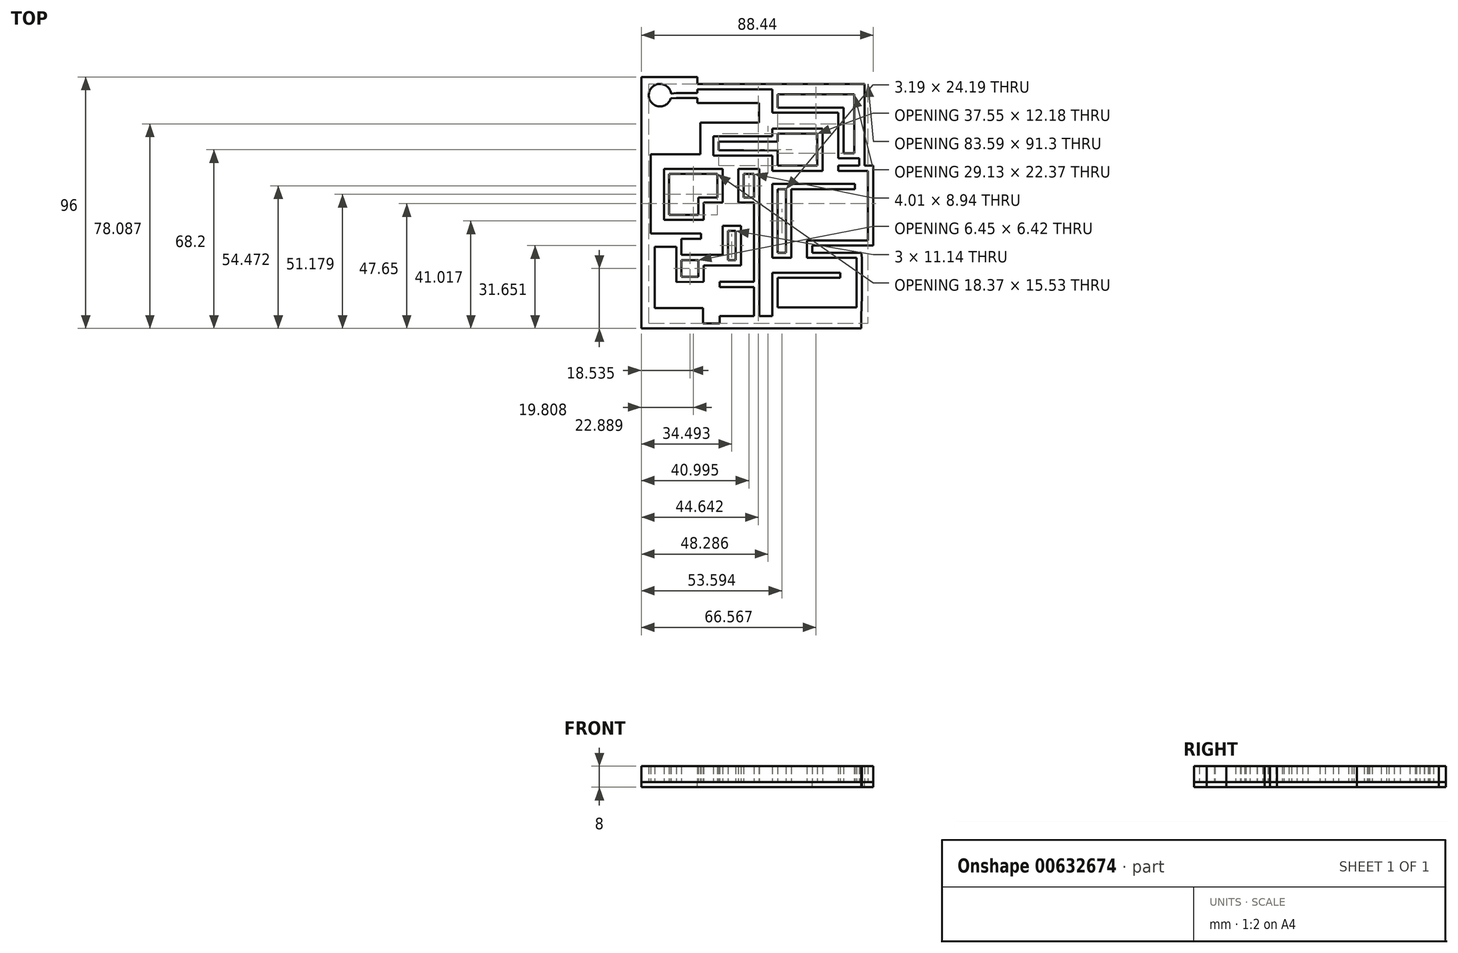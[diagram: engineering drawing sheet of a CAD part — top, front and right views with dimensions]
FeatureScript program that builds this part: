
annotation { "Feature Type Name" : "Feature", "Feature Type Description" : "" }
export const myFeature = defineFeature(function(context is Context, id is Id, definition is map)
    precondition{}
    {
        {
            var Q0;
            Q0=qCreatedBy(makeId("Top.planeOp"),FACE);
            var sketch = newSketch(context, id + "F0", { "sketchPlane" : qUnion([Q0])});
            skLineSegment(sketch, "E0.bottom", {"start": v(-50, 50) * mm, "end": v(50, 50) * mm});
            skLineSegment(sketch, "E0.top", {"start": v(-50, -50) * mm, "end": v(-26.52, -50) * mm});
            skLineSegment(sketch, "E0.left", {"start": v(-50, 50) * mm, "end": v(-50, -50) * mm});
            skPoint(sketch, "E0.middle", {"position": v(0, 0) * mm});
            skLineSegment(sketch, "E1", {"start": v(35.85, -48) * mm, "end": v(35.85, -43.22) * mm});
            skLineSegment(sketch, "E2.5", {"start": v(2, 43.27) * mm, "end": v(2, 34.3) * mm});
            skLineSegment(sketch, "E2.6", {"start": v(2, 25.31) * mm, "end": v(-20.49, 25.31) * mm});
            skLineSegment(sketch, "E3", {"start": v(-20.49, 25.31) * mm, "end": v(-20.49, 17.94) * mm});
            skLineSegment(sketch, "E4", {"start": v(-20.49, 17.94) * mm, "end": v(-2.51, 17.94) * mm});
            skLineSegment(sketch, "E5", {"start": v(-2.51, 17.94) * mm, "end": v(2, 17.94) * mm});
            skLineSegment(sketch, "E6", {"start": v(2, 17.94) * mm, "end": v(2, 12.1) * mm});
            skLineSegment(sketch, "E7", {"start": v(2, 12.1) * mm, "end": v(21.06, 12.1) * mm});
            skLineSegment(sketch, "E8", {"start": v(38.44, 12.1) * mm, "end": v(38.44, 3.69) * mm});
            skLineSegment(sketch, "E9.1", {"start": v(-3, 13.1) * mm, "end": v(-3, 12.94) * mm});
            skLineSegment(sketch, "E9.5", {"start": v(-26.62, 38.07) * mm, "end": v(-3.2, 38.07) * mm});
            skLineSegment(sketch, "E9.6", {"start": v(-3.2, 38.07) * mm, "end": v(-3.2, 30.51) * mm});
            skLineSegment(sketch, "E9.7", {"start": v(-3.2, 30.51) * mm, "end": v(-25.49, 30.51) * mm});
            skLineSegment(sketch, "E10", {"start": v(-25.29, 12.94) * mm, "end": v(-17, 12.94) * mm});
            skLineSegment(sketch, "E11", {"start": v(-28.73, -6.59) * mm, "end": v(-39.38, -6.59) * mm});
            skLineSegment(sketch, "E12", {"start": v(-39.38, -6.59) * mm, "end": v(-39.38, 12.94) * mm});
            skLineSegment(sketch, "E13", {"start": v(2, -43.22) * mm, "end": v(-18.08, -43.22) * mm});
            skLineSegment(sketch, "E14", {"start": v(-18.08, -43.22) * mm, "end": v(-18.08, -48) * mm});
            skLineSegment(sketch, "E15", {"start": v(-3, 13.1) * mm, "end": v(-3, 0) * mm});
            skLineSegment(sketch, "E16", {"start": v(-3, 0) * mm, "end": v(-11, 0) * mm});
            skLineSegment(sketch, "E17", {"start": v(-24.24, 0) * mm, "end": v(-24.24, -2.75) * mm});
            skLineSegment(sketch, "E18", {"start": v(-3, -2.75) * mm, "end": v(-3, -30.2) * mm});
            skLineSegment(sketch, "E19", {"start": v(-3, -30.2) * mm, "end": v(-8.04, -30.2) * mm});
            skLineSegment(sketch, "E20", {"start": v(-24.52, -42.24) * mm, "end": v(-24.52, -43.24) * mm});
            skLineSegment(sketch, "E21", {"start": v(2, 7.1) * mm, "end": v(2, -21.08) * mm});
            skLineSegment(sketch, "E22", {"start": v(2, -26.68) * mm, "end": v(2, -43.22) * mm});
            skLineSegment(sketch, "E23", {"start": v(2, -21.08) * mm, "end": v(9.19, -21.08) * mm});
            skLineSegment(sketch, "E24", {"start": v(34.05, -21.08) * mm, "end": v(34.05, -26.68) * mm});
            skLineSegment(sketch, "E25", {"start": v(2, -26.68) * mm, "end": v(27.88, -26.68) * mm});
            skLineSegment(sketch, "E26", {"start": v(27.88, -26.68) * mm, "end": v(27.88, -28.68) * mm});
            skLineSegment(sketch, "E27", {"start": v(34.05, -26.68) * mm, "end": v(34.05, -35.77) * mm});
            skLineSegment(sketch, "E28", {"start": v(34.05, -35.77) * mm, "end": v(34.05, -40) * mm});
            skLineSegment(sketch, "E29", {"start": v(34.05, -40) * mm, "end": v(4, -40) * mm});
            skLineSegment(sketch, "E30.1", {"start": v(-44.38, -11.59) * mm, "end": v(-44.38, 18.44) * mm});
            skLineSegment(sketch, "E31.0", {"start": v(-25.49, 25.31) * mm, "end": v(-25.49, 18.44) * mm});
            skLineSegment(sketch, "E32", {"start": v(-25.49, 25.31) * mm, "end": v(-25.49, 30.51) * mm});
            skLineSegment(sketch, "E33", {"start": v(-17, -8.78) * mm, "end": v(-17, -14.81) * mm});
            skLineSegment(sketch, "E34", {"start": v(-44.92, -14.81) * mm, "end": v(-44.92, -35.22) * mm});
            skLineSegment(sketch, "E35", {"start": v(-44.92, -35.22) * mm, "end": v(-44.92, -42.24) * mm});
            skLineSegment(sketch, "E36", {"start": v(-44.92, -42.24) * mm, "end": v(-24.52, -42.24) * mm});
            skLineSegment(sketch, "E37", {"start": v(-17, -14.81) * mm, "end": v(-17, -19.9) * mm});
            skLineSegment(sketch, "E38", {"start": v(-17, -19.9) * mm, "end": v(-34.69, -19.9) * mm});
            skLineSegment(sketch, "E39", {"start": v(-34.69, -19.9) * mm, "end": v(-34.69, -30.35) * mm});
            skLineSegment(sketch, "E40", {"start": v(-34.69, -30.35) * mm, "end": v(-24.52, -30.2) * mm});
            skLineSegment(sketch, "E41", {"start": v(2, 12.1) * mm, "end": v(2, 7.1) * mm});
            skLineSegment(sketch, "E42", {"start": v(-17, -8.78) * mm, "end": v(-10, -8.78) * mm});
            skLineSegment(sketch, "E43", {"start": v(-10, -8.78) * mm, "end": v(-10, -23.92) * mm});
            skLineSegment(sketch, "E44", {"start": v(-10, -23.92) * mm, "end": v(-24.24, -23.92) * mm});
            skLineSegment(sketch, "E45", {"start": v(-34.69, -19.9) * mm, "end": v(-34.69, -14.81) * mm});
            skLineSegment(sketch, "E46", {"start": v(-8.04, -30.2) * mm, "end": v(-18.08, -30.2) * mm});
            skLineSegment(sketch, "E47", {"start": v(9.19, 5.1) * mm, "end": v(9.19, -21.08) * mm});
            skLineSegment(sketch, "E48.trimOffspring", {"start": v(15.19, -21.08) * mm, "end": v(34.05, -21.08) * mm});
            skLineSegment(sketch, "E49", {"start": v(2, 34.3) * mm, "end": v(27.06, 34.3) * mm});
            skLineSegment(sketch, "E50", {"start": v(27.06, 34.3) * mm, "end": v(27.06, 16.9) * mm});
            skLineSegment(sketch, "E51.0", {"start": v(21.06, 28.3) * mm, "end": v(21.06, 12.1) * mm});
            skLineSegment(sketch, "E51.1", {"start": v(2, 28.3) * mm, "end": v(21.06, 28.3) * mm});
            skLineSegment(sketch, "E52.trimOffspring", {"start": v(2, 28.3) * mm, "end": v(2, 25.31) * mm});
            skLineSegment(sketch, "E53.trimOffspring", {"start": v(27.06, 12.1) * mm, "end": v(38.44, 12.1) * mm});
            skLineSegment(sketch, "E54", {"start": v(-26.62, 38.07) * mm, "end": v(-26.62, 39.2) * mm});
            skLineSegment(sketch, "E55", {"start": v(2, 43.27) * mm, "end": v(-20.5, 43.27) * mm});
            skLineSegment(sketch, "E56", {"start": v(35.1, 16.9) * mm, "end": v(27.06, 16.9) * mm});
            skLineSegment(sketch, "E57.trimOffspring", {"start": v(27.06, 12.1) * mm, "end": v(27.06, 12.08) * mm});
            skLineSegment(sketch, "E58", {"start": v(38.44, 3.69) * mm, "end": v(38.44, -14.38) * mm});
            skLineSegment(sketch, "E59", {"start": v(38.44, -14.38) * mm, "end": v(15.19, -14.38) * mm});
            skLineSegment(sketch, "E60.trimOffspring", {"start": v(15.19, -14.38) * mm, "end": v(15.19, -21.08) * mm});
            skLineSegment(sketch, "E61", {"start": v(-17, 0) * mm, "end": v(-17, 12.94) * mm});
            skLineSegment(sketch, "E62.0", {"start": v(-11, 0) * mm, "end": v(-11, 12.94) * mm});
            skLineSegment(sketch, "E63.trimOffspring", {"start": v(-17, 0) * mm, "end": v(-24.24, 0) * mm});
            skLineSegment(sketch, "E64.trimOffspring", {"start": v(-11, 12.94) * mm, "end": v(-3, 12.94) * mm});
            skLineSegment(sketch, "E65", {"start": v(-28.73, -6.59) * mm, "end": v(-24.24, -6.59) * mm});
            skLineSegment(sketch, "E66.0", {"start": v(-27.49, 25.31) * mm, "end": v(-27.49, 20.44) * mm});
            skLineSegment(sketch, "E66.1", {"start": v(-27.49, 25.31) * mm, "end": v(-27.49, 32.51) * mm});
            skLineSegment(sketch, "E66.2", {"start": v(-28.62, 36.07) * mm, "end": v(-28.62, 38.07) * mm});
            skLineSegment(sketch, "E66.3", {"start": v(-28.62, 36.07) * mm, "end": v(-5.2, 36.07) * mm});
            skLineSegment(sketch, "E66.4", {"start": v(-5.2, 36.07) * mm, "end": v(-5.2, 32.51) * mm});
            skLineSegment(sketch, "E66.5", {"start": v(-5.2, 32.51) * mm, "end": v(-27.49, 32.51) * mm});
            skCircle(sketch, "E67", {"center": v(42.5, -41.37) * mm, "radius": 1.37 * mm});
            skCircle(sketch, "E68", {"center": v(42.5, -41.37) * mm, "radius": 0.87 * mm});
            skLineSegment(sketch, "E69.0", {"start": v(-46.38, -13.59) * mm, "end": v(-46.38, 18.44) * mm});
            skLineSegment(sketch, "E70.4", {"start": v(-46.38, -44.24) * mm, "end": v(-26.52, -44.24) * mm});
            skLineSegment(sketch, "E71", {"start": v(-26.52, -50) * mm, "end": v(-24.52, -50) * mm});
            skCircle(sketch, "E72", {"center": v(42.5, -41.37) * mm, "radius": 2.87 * mm});
            skLineSegment(sketch, "E73", {"start": v(-46.38, 18.44) * mm, "end": v(-46.38, 20.47) * mm});
            skLineSegment(sketch, "E74", {"start": v(-46.38, -13.59) * mm, "end": v(-46.38, -44.24) * mm});
            skPoint(sketch, "E75.orphan", {"position": v(-46.92, -44.24) * mm});
            skLineSegment(sketch, "E76", {"start": v(-44.32, 20.44) * mm, "end": v(-46.38, 20.47) * mm});
            skLineSegment(sketch, "E77", {"start": v(-44.32, 20.44) * mm, "end": v(-27.49, 20.44) * mm});
            skLineSegment(sketch, "E78", {"start": v(-24.24, -6.59) * mm, "end": v(-24.24, -2.75) * mm});
            skLineSegment(sketch, "E79.trimOffspring", {"start": v(-25.49, 17.95) * mm, "end": v(-25.49, 17.94) * mm});
            skLineSegment(sketch, "E80.0", {"start": v(-48, 48) * mm, "end": v(-28.62, 48) * mm});
            skLineSegment(sketch, "E80.1", {"start": v(-48, 48) * mm, "end": v(-48, -48) * mm});
            skLineSegment(sketch, "E80.2", {"start": v(-48, -48) * mm, "end": v(48, -48) * mm});
            skLineSegment(sketch, "E80.3", {"start": v(48, 48) * mm, "end": v(48, -48) * mm});
            skLineSegment(sketch, "E81.trimOffspring", {"start": v(-26.62, 48) * mm, "end": v(48, 48) * mm});
            skLineSegment(sketch, "E82", {"start": v(-44.38, 18.44) * mm, "end": v(-25.49, 18.44) * mm});
            skLineSegment(sketch, "E83.0", {"start": v(2, 45.27) * mm, "end": v(-20.5, 45.27) * mm});
            skLineSegment(sketch, "E83.1", {"start": v(2, 45.27) * mm, "end": v(12.72, 45.27) * mm});
            skLineSegment(sketch, "E83.2", {"start": v(37.1, 45.27) * mm, "end": v(37.1, 16.9) * mm});
            skLineSegment(sketch, "E83.3", {"start": v(34.15, 45.27) * mm, "end": v(37.1, 45.27) * mm});
            skLineSegment(sketch, "E83.4", {"start": v(15.13, 45.27) * mm, "end": v(34.15, 45.27) * mm});
            skLineSegment(sketch, "E83.5", {"start": v(12.72, 45.27) * mm, "end": v(15.13, 45.27) * mm});
            skLineSegment(sketch, "E84", {"start": v(37.1, 12.08) * mm, "end": v(37.1, 12.1) * mm});
            skLineSegment(sketch, "E85.1", {"start": v(-37.38, -4.59) * mm, "end": v(-37.38, 10.94) * mm});
            skLineSegment(sketch, "E85.2", {"start": v(-25.32, 10.94) * mm, "end": v(-19, 10.94) * mm});
            skLineSegment(sketch, "E85.3", {"start": v(-28.73, -4.59) * mm, "end": v(-37.38, -4.59) * mm});
            skLineSegment(sketch, "E85.4", {"start": v(-28.73, -4.59) * mm, "end": v(-26.24, -4.59) * mm});
            skLineSegment(sketch, "E85.5", {"start": v(-19, 2) * mm, "end": v(-19, 10.94) * mm});
            skLineSegment(sketch, "E85.6", {"start": v(-19, 2) * mm, "end": v(-26.24, 2) * mm});
            skLineSegment(sketch, "E85.7", {"start": v(-26.24, 2) * mm, "end": v(-26.24, -2.75) * mm});
            skLineSegment(sketch, "E85.8", {"start": v(-26.24, -4.59) * mm, "end": v(-26.24, -2.75) * mm});
            skLineSegment(sketch, "E86", {"start": v(37.1, 12.1) * mm, "end": v(37.1, 12.08) * mm});
            skLineSegment(sketch, "E87.0", {"start": v(19.06, 22.3) * mm, "end": v(19.06, 14.1) * mm});
            skLineSegment(sketch, "E87.2", {"start": v(-2.51, 19.94) * mm, "end": v(4, 19.94) * mm});
            skLineSegment(sketch, "E87.3", {"start": v(4, 19.94) * mm, "end": v(4, 14.1) * mm});
            skLineSegment(sketch, "E87.4", {"start": v(4, 14.1) * mm, "end": v(19.06, 14.1) * mm});
            skLineSegment(sketch, "E88.0", {"start": v(-18.49, 23.31) * mm, "end": v(-18.49, 17.94) * mm});
            skLineSegment(sketch, "E88.1", {"start": v(4, 23.31) * mm, "end": v(-18.49, 23.31) * mm});
            skLineSegment(sketch, "E88.2", {"start": v(4, 26.3) * mm, "end": v(4, 23.31) * mm});
            skLineSegment(sketch, "E89.0", {"start": v(4, 26.3) * mm, "end": v(19.06, 26.3) * mm});
            skLineSegment(sketch, "E90.0", {"start": v(-18.49, 19.94) * mm, "end": v(-2.51, 19.94) * mm});
            skLineSegment(sketch, "E91.0", {"start": v(27.06, 14.1) * mm, "end": v(35.1, 14.1) * mm});
            skLineSegment(sketch, "E92.0", {"start": v(40.44, 3.69) * mm, "end": v(40.44, -14.38) * mm});
            skLineSegment(sketch, "E92.1", {"start": v(40.44, 12.1) * mm, "end": v(40.44, 3.69) * mm});
            skLineSegment(sketch, "E93", {"start": v(40.44, 14.1) * mm, "end": v(40.44, 12.1) * mm});
            skLineSegment(sketch, "E94.0", {"start": v(17.19, -16.38) * mm, "end": v(17.19, -19.08) * mm});
            skLineSegment(sketch, "E94.1", {"start": v(38.44, -16.38) * mm, "end": v(17.19, -16.38) * mm});
            skLineSegment(sketch, "E95.0", {"start": v(17.19, -19.08) * mm, "end": v(34.05, -19.08) * mm});
            skLineSegment(sketch, "E96", {"start": v(40.44, -14.38) * mm, "end": v(40.44, -16.38) * mm});
            skLineSegment(sketch, "E97", {"start": v(40.44, -16.38) * mm, "end": v(38.44, -16.38) * mm});
            skLineSegment(sketch, "E98.1", {"start": v(36.05, -26.68) * mm, "end": v(36.05, -35.77) * mm});
            skLineSegment(sketch, "E98.2", {"start": v(36.05, -21.08) * mm, "end": v(36.05, -26.68) * mm});
            skLineSegment(sketch, "E99", {"start": v(34.05, -19.08) * mm, "end": v(35.9, -19.08) * mm});
            skLineSegment(sketch, "E100", {"start": v(35.9, -19.08) * mm, "end": v(36.05, -21.08) * mm});
            skLineSegment(sketch, "E101", {"start": v(2, -43.22) * mm, "end": v(35.85, -43.22) * mm});
            skLineSegment(sketch, "E102", {"start": v(36.05, -35.77) * mm, "end": v(35.85, -43.22) * mm});
            skLineSegment(sketch, "E103.0", {"start": v(33.85, -48) * mm, "end": v(33.85, -45.22) * mm});
            skLineSegment(sketch, "E103.1", {"start": v(2, -45.22) * mm, "end": v(33.85, -45.22) * mm});
            skLineSegment(sketch, "E103.2", {"start": v(2, -45.22) * mm, "end": v(-16.08, -45.22) * mm});
            skLineSegment(sketch, "E103.3", {"start": v(-16.08, -45.22) * mm, "end": v(-16.08, -48) * mm});
            skCircle(sketch, "E104", {"center": v(42.5, -41.37) * mm, "radius": 4.65 * mm});
            skCircle(sketch, "E105", {"center": v(42.5, -41.37) * mm, "radius": 4.04 * mm});
            skCircle(sketch, "E106", {"center": v(42.5, -41.37) * mm, "radius": 2.12 * mm});
            skLineSegment(sketch, "E107.0", {"start": v(-32.69, -28.32) * mm, "end": v(-26.44, -28.24) * mm});
            skLineSegment(sketch, "E107.1", {"start": v(-32.69, -21.9) * mm, "end": v(-32.69, -28.32) * mm});
            skLineSegment(sketch, "E108.2", {"start": v(-15, -10.78) * mm, "end": v(-12, -10.78) * mm});
            skLineSegment(sketch, "E109.0", {"start": v(-12, -10.78) * mm, "end": v(-12, -21.92) * mm});
            skLineSegment(sketch, "E110", {"start": v(-24.24, -24.07) * mm, "end": v(-24.24, -30.19) * mm});
            skLineSegment(sketch, "E111", {"start": v(-24.24, -30.19) * mm, "end": v(-24.52, -30.2) * mm});
            skLineSegment(sketch, "E112", {"start": v(-24.24, -24.07) * mm, "end": v(-24.24, -23.92) * mm});
            skLineSegment(sketch, "E113.0", {"start": v(-26.24, -24.07) * mm, "end": v(-26.24, -28.24) * mm});
            skLineSegment(sketch, "E114", {"start": v(-26.26, -23.92) * mm, "end": v(-26.24, -24.07) * mm});
            skLineSegment(sketch, "E115", {"start": v(-26.44, -28.24) * mm, "end": v(-26.24, -28.24) * mm});
            skLineSegment(sketch, "E116", {"start": v(27.06, 14.1) * mm, "end": v(27.06, 12.1) * mm});
            skLineSegment(sketch, "E117.0", {"start": v(-10.04, -32.2) * mm, "end": v(-18.08, -32.2) * mm});
            skLineSegment(sketch, "E117.1", {"start": v(-10.04, -43.22) * mm, "end": v(-10.04, -32.2) * mm});
            skLineSegment(sketch, "E118", {"start": v(-18.08, -30.2) * mm, "end": v(-18.08, -32.2) * mm});
            skLineSegment(sketch, "E119", {"start": v(-3, -2.75) * mm, "end": v(-3, 0) * mm});
            skPoint(sketch, "E120.start.orphan", {"position": v(-8.04, -43.22) * mm});
            skLineSegment(sketch, "E121", {"start": v(-3, -30.2) * mm, "end": v(-3, -43.22) * mm});
            skLineSegment(sketch, "E122.0", {"start": v(-5, -2.75) * mm, "end": v(-5, -30.2) * mm});
            skLineSegment(sketch, "E123", {"start": v(-5, -2.75) * mm, "end": v(-5, 0) * mm});
            skLineSegment(sketch, "E124", {"start": v(-12, -21.92) * mm, "end": v(-15, -21.92) * mm});
            skPoint(sketch, "E108.0.end.orphan", {"position": v(-15, -19.9) * mm});
            skLineSegment(sketch, "E125", {"start": v(-15, -10.78) * mm, "end": v(-15, -21.92) * mm});
            skLineSegment(sketch, "E126", {"start": v(-32.69, -21.9) * mm, "end": v(-26.24, -21.9) * mm});
            skLineSegment(sketch, "E127", {"start": v(-26.24, -21.9) * mm, "end": v(-26.26, -23.92) * mm});
            skLineSegment(sketch, "E128.0", {"start": v(-32.69, -19.9) * mm, "end": v(-32.69, -14.81) * mm});
            skLineSegment(sketch, "E129.0", {"start": v(33.44, 5.1) * mm, "end": v(28.44, 5.1) * mm});
            skLineSegment(sketch, "E130.0", {"start": v(4, 5.1) * mm, "end": v(4, -19.08) * mm});
            skLineSegment(sketch, "E130.1", {"start": v(4, -19.08) * mm, "end": v(7.19, -19.08) * mm});
            skLineSegment(sketch, "E130.2", {"start": v(7.19, 5.1) * mm, "end": v(7.19, -19.08) * mm});
            skLineSegment(sketch, "E131.0", {"start": v(30.44, 5.1) * mm, "end": v(28.44, 5.1) * mm});
            skLineSegment(sketch, "E132.trimOffspring", {"start": v(7.19, 5.1) * mm, "end": v(4, 5.1) * mm});
            skLineSegment(sketch, "E133.0", {"start": v(7, 36.3) * mm, "end": v(29.06, 36.3) * mm});
            skLineSegment(sketch, "E133.1", {"start": v(29.06, 36.3) * mm, "end": v(29.06, 18.9) * mm});
            skLineSegment(sketch, "E133.2", {"start": v(33.13, 18.9) * mm, "end": v(29.06, 18.9) * mm});
            skLineSegment(sketch, "E134.0", {"start": v(4, 41.27) * mm, "end": v(4, 36.3) * mm});
            skLineSegment(sketch, "E134.1", {"start": v(4, 41.27) * mm, "end": v(12.72, 41.27) * mm});
            skLineSegment(sketch, "E134.2", {"start": v(12.72, 41.27) * mm, "end": v(15.13, 41.27) * mm});
            skLineSegment(sketch, "E134.3", {"start": v(15.13, 41.27) * mm, "end": v(33.13, 41.27) * mm});
            skLineSegment(sketch, "E135.0", {"start": v(33.13, 41.27) * mm, "end": v(33.13, 18.9) * mm});
            skLineSegment(sketch, "E136", {"start": v(7, 36.3) * mm, "end": v(4, 36.3) * mm});
            skLineSegment(sketch, "E137.0", {"start": v(-9, 10.94) * mm, "end": v(-5, 10.94) * mm});
            skLineSegment(sketch, "E137.1", {"start": v(-9, 2) * mm, "end": v(-9, 10.94) * mm});
            skLineSegment(sketch, "E137.2", {"start": v(-5, 2) * mm, "end": v(-9, 2) * mm});
            skLineSegment(sketch, "E138.0", {"start": v(-5, 13.1) * mm, "end": v(-5, 12.94) * mm});
            skLineSegment(sketch, "E139.trimOffspring", {"start": v(-5, 10.94) * mm, "end": v(-5, 2) * mm});
            skLineSegment(sketch, "E140", {"start": v(19.06, 22.3) * mm, "end": v(19.06, 26.3) * mm});
            skLineSegment(sketch, "E141.0", {"start": v(-42.92, -16.81) * mm, "end": v(-42.92, -35.22) * mm});
            skLineSegment(sketch, "E141.1", {"start": v(-34.69, -16.81) * mm, "end": v(-42.92, -16.81) * mm});
            skLineSegment(sketch, "E142.0", {"start": v(-42.92, -40.24) * mm, "end": v(-24.52, -40.24) * mm});
            skLineSegment(sketch, "E142.1", {"start": v(-42.92, -35.22) * mm, "end": v(-42.92, -40.24) * mm});
            skLineSegment(sketch, "E143", {"start": v(-24.52, -42.24) * mm, "end": v(-24.52, -40.24) * mm});
            skLineSegment(sketch, "E144.0", {"start": v(-25.24, -13.81) * mm, "end": v(-44.92, -13.81) * mm});
            skLineSegment(sketch, "E145.0", {"start": v(-25.24, -11.59) * mm, "end": v(-25.24, -13.81) * mm});
            skLineSegment(sketch, "E146.0", {"start": v(4, -28.68) * mm, "end": v(27.88, -28.68) * mm});
            skLineSegment(sketch, "E147.0", {"start": v(-5, -32.2) * mm, "end": v(-5, -43.22) * mm});
            skLineSegment(sketch, "E148.0", {"start": v(-8.04, -32.2) * mm, "end": v(-18.08, -32.2) * mm});
            skLineSegment(sketch, "E148.1", {"start": v(-5, -32.2) * mm, "end": v(-8.04, -32.2) * mm});
            skLineSegment(sketch, "E149", {"start": v(-44.92, -14.81) * mm, "end": v(-44.92, -13.81) * mm});
            skLineSegment(sketch, "E150", {"start": v(-34.69, -14.81) * mm, "end": v(-34.69, -13.81) * mm});
            skLineSegment(sketch, "E151", {"start": v(-32.69, -14.81) * mm, "end": v(-32.69, -13.81) * mm});
            skLineSegment(sketch, "E152.trimOffspring", {"start": v(37.1, 14.1) * mm, "end": v(40.44, 14.1) * mm});
            skLineSegment(sketch, "E153.trimOffspring", {"start": v(35.13, 12.1) * mm, "end": v(35.13, 12.08) * mm});
            skLineSegment(sketch, "E154.trimOffspring", {"start": v(37.1, 14.1) * mm, "end": v(37.1, 16.9) * mm});
            skArc(sketch, "E155", {"start": v(-35.02, 43.27) * mm, "mid": v(-47.16, 41.4) * mm, "end": v(-35.34, 38.07) * mm});
            skLineSegment(sketch, "E156", {"start": v(-34.66, 41.87) * mm, "end": v(-28.62, 41.87) * mm});
            skLineSegment(sketch, "E157.trimOffspring", {"start": v(-28.62, 43.27) * mm, "end": v(-28.62, 48) * mm});
            skLineSegment(sketch, "E158", {"start": v(-26.62, 41.93) * mm, "end": v(-26.62, 43.27) * mm});
            skLineSegment(sketch, "E159.0", {"start": v(-34.66, 39.87) * mm, "end": v(-28.62, 39.87) * mm});
            skLineSegment(sketch, "E160", {"start": v(-26.62, 39.2) * mm, "end": v(-26.62, 39.87) * mm});
            skLineSegment(sketch, "E161.0", {"start": v(35.1, 14.1) * mm, "end": v(35.1, 16.9) * mm});
            skLineSegment(sketch, "E162.0", {"start": v(4, -28.68) * mm, "end": v(4, -40) * mm});
            skLineSegment(sketch, "E163.0", {"start": v(-25.24, -11.81) * mm, "end": v(-44.38, -11.81) * mm});
            skLineSegment(sketch, "E164", {"start": v(33.44, 7.1) * mm, "end": v(33.44, 5.1) * mm});
            skLineSegment(sketch, "E165.0", {"start": v(7.19, 7.1) * mm, "end": v(4, 7.1) * mm});
            skLineSegment(sketch, "E166.0", {"start": v(30.44, 7.1) * mm, "end": v(9.19, 7.1) * mm});
            skLineSegment(sketch, "E167", {"start": v(2, 7.1) * mm, "end": v(4, 7.1) * mm});
            skLineSegment(sketch, "E168", {"start": v(7.19, 7.1) * mm, "end": v(9.19, 7.1) * mm});
            skLineSegment(sketch, "E169", {"start": v(30.44, 7.1) * mm, "end": v(33.44, 7.1) * mm});
            skLineSegment(sketch, "E170.trimOffspring", {"start": v(17.19, 5.1) * mm, "end": v(9.19, 5.1) * mm});
            skLineSegment(sketch, "E171.trimOffspring", {"start": v(17.19, 5.1) * mm, "end": v(15.19, 5.1) * mm});
            skLineSegment(sketch, "E172", {"start": v(17.19, 5.1) * mm, "end": v(28.44, 5.1) * mm});
            skArc(sketch, "E173.0", {"start": v(-36.64, 41.6) * mm, "mid": v(-45.15, 41.36) * mm, "end": v(-36.79, 39.77) * mm});
            skLineSegment(sketch, "E174", {"start": v(-28.62, 41.87) * mm, "end": v(-26.62, 41.87) * mm});
            skLineSegment(sketch, "E175", {"start": v(-26.62, 41.87) * mm, "end": v(-26.62, 41.93) * mm});
            skLineSegment(sketch, "E176.0", {"start": v(-28.62, 39.87) * mm, "end": v(-26.62, 39.87) * mm});
            skLineSegment(sketch, "E177", {"start": v(-44.38, -11.59) * mm, "end": v(-44.38, -11.81) * mm});
            skLineSegment(sketch, "E178", {"start": v(-26.52, -44.24) * mm, "end": v(-24.52, -44.24) * mm});
            skLineSegment(sketch, "E179", {"start": v(-24.52, -44.24) * mm, "end": v(-24.52, -43.24) * mm});
            skLineSegment(sketch, "E180", {"start": v(-25.32, 10.94) * mm, "end": v(-37.38, 10.94) * mm});
            skLineSegment(sketch, "E181.0", {"start": v(-25.32, 12.94) * mm, "end": v(-37.38, 12.94) * mm});
            skLineSegment(sketch, "E182", {"start": v(-37.38, 12.94) * mm, "end": v(-39.38, 12.94) * mm});
            skLineSegment(sketch, "E183", {"start": v(-36.64, 41.6) * mm, "end": v(-34.66, 41.87) * mm});
            skLineSegment(sketch, "E184", {"start": v(-36.79, 39.77) * mm, "end": v(-34.66, 39.87) * mm});
            skLineSegment(sketch, "E185", {"start": v(-25.32, 12.94) * mm, "end": v(-25.29, 12.94) * mm});
            skLineSegment(sketch, "E186", {"start": v(-28.62, 48) * mm, "end": v(-26.62, 48) * mm});
            skLineSegment(sketch, "E187.trimOffspring", {"start": v(-24.52, -50) * mm, "end": v(50, -50) * mm});
            skLineSegment(sketch, "E188.trimOffspring", {"start": v(42.13, -46) * mm, "end": v(42.88, -46) * mm});
            skLineSegment(sketch, "E189", {"start": v(-20.5, 45.27) * mm, "end": v(-26.62, 45.27) * mm});
            skLineSegment(sketch, "E190.0", {"start": v(-20.5, 43.27) * mm, "end": v(-26.62, 43.27) * mm});
            skLineSegment(sketch, "E191", {"start": v(-24.52, -44.24) * mm, "end": v(-24.52, -48) * mm});
            skLineSegment(sketch, "E192.0", {"start": v(-26.52, -44.24) * mm, "end": v(-26.52, -48) * mm});
            skLineSegment(sketch, "E193.0", {"start": v(-24.52, -46) * mm, "end": v(-18.08, -46) * mm});
            skLineSegment(sketch, "E194", {"start": v(-28.62, 38.07) * mm, "end": v(-35.34, 38.07) * mm});
            skLineSegment(sketch, "E195", {"start": v(-28.62, 43.27) * mm, "end": v(-35.02, 43.27) * mm});
            skPoint(sketch, "E196.start.orphan", {"position": v(-28.62, 39.2) * mm});
            skLineSegment(sketch, "E197.trimOffspring", {"start": v(-26.62, 45.27) * mm, "end": v(-26.62, 48) * mm});
            skSolve(sketch);
        }
        {
            var Q0;
            {var subQ0=sQuery(id+"F0.wireOp",EDGE,"E1");var subQ1=sQuery(id+"F0.wireOp",EDGE,"E0.top");var subQ2=makeQuery(id+"F0.imprint","INTERSECT",VERTEX,{"derivedFrom":[subQ1,subQ0]});Q0=makeQuery(id+"F0.imprint","IMPRINT",FACE,{"disambiguationData":[TD([[makeQuery(id+"F0.imprint","IMPRINT",EDGE,{"disambiguationData":[TD([[subQ2,1.0]])],"derivedFrom":subQ1}),1.0]])]});}
            var Q1;
            {var subQ0=sQuery(id+"F0.wireOp",EDGE,"E14");var subQ1=sQuery(id+"F0.wireOp",EDGE,"E0.top");var subQ2=makeQuery(id+"F0.imprint","INTERSECT",VERTEX,{"derivedFrom":[subQ1,subQ0]});Q1=makeQuery(id+"F0.imprint","IMPRINT",FACE,{"disambiguationData":[TD([[makeQuery(id+"F0.imprint","IMPRINT",EDGE,{"disambiguationData":[TD([[subQ2,-1.0]])],"derivedFrom":subQ1}),1.0]])]});}
            var Q2;
            {var subQ0=sQuery(id+"F0.wireOp",EDGE,"E103.0");var subQ1=sQuery(id+"F0.wireOp",EDGE,"E0.top");var subQ2=makeQuery(id+"F0.imprint","INTERSECT",VERTEX,{"derivedFrom":[subQ1,subQ0]});Q2=makeQuery(id+"F0.imprint","IMPRINT",FACE,{"disambiguationData":[TD([[makeQuery(id+"F0.imprint","IMPRINT",EDGE,{"disambiguationData":[TD([[subQ2,1.0]])],"derivedFrom":subQ1}),1.0]])]});}
            var Q3;
            {var subQ5=sQuery(id+"F0.wireOp",EDGE,"E101");Q3=makeQuery(id+"F0.imprint","IMPRINT",FACE,{"disambiguationData":[TD([[makeQuery(id+"F0.imprint","IMPRINT",EDGE,{"derivedFrom":subQ5}),-1.0]])]});}
            var Q4;
            Q4=makeQuery(id+"F0.imprint","IMPRINT",FACE,{"disambiguationData":[TD([[makeQuery(id+"F0.imprint","IMPRINT",EDGE,{"derivedFrom":sQuery(id+"F0.wireOp",EDGE,"E9.5")}),-1.0]])]});
            var Q5;
            Q5=makeQuery(id+"F0.imprint","IMPRINT",FACE,{"disambiguationData":[TD([[makeQuery(id+"F0.imprint","IMPRINT",EDGE,{"derivedFrom":sQuery(id+"F0.wireOp",EDGE,"E10")}),-1.0]])]});
            var Q6;
            Q6=makeQuery(id+"F0.imprint","IMPRINT",FACE,{"disambiguationData":[TD([[makeQuery(id+"F0.imprint","IMPRINT",EDGE,{"derivedFrom":sQuery(id+"F0.wireOp",EDGE,"E2.6")}),1.0]])]});
            var Q7;
            {var subQ0=sQuery(id+"F0.wireOp",EDGE,"E62.0");Q7=makeQuery(id+"F0.imprint","IMPRINT",FACE,{"disambiguationData":[TD([[makeQuery(id+"F0.imprint","IMPRINT",EDGE,{"derivedFrom":subQ0}),-1.0]])]});}
            var Q8;
            {var subQ2=sQuery(id+"F0.wireOp",EDGE,"E18");Q8=makeQuery(id+"F0.imprint","IMPRINT",FACE,{"disambiguationData":[TD([[makeQuery(id+"F0.imprint","IMPRINT",EDGE,{"derivedFrom":subQ2}),-1.0]])]});}
            var Q9;
            Q9=makeQuery(id+"F0.imprint","IMPRINT",FACE,{"disambiguationData":[TD([[makeQuery(id+"F0.imprint","IMPRINT",EDGE,{"derivedFrom":sQuery(id+"F0.wireOp",EDGE,"E33")}),1.0]])]});
            var Q10;
            Q10=makeQuery(id+"F0.imprint","IMPRINT",FACE,{"disambiguationData":[TD([[makeQuery(id+"F0.imprint","IMPRINT",EDGE,{"derivedFrom":sQuery(id+"F0.wireOp",EDGE,"E34")}),1.0]])]});
            var Q11;
            {var subQ5=sQuery(id+"F0.wireOp",EDGE,"E128.0");Q11=makeQuery(id+"F0.imprint","IMPRINT",FACE,{"disambiguationData":[TD([[makeQuery(id+"F0.imprint","IMPRINT",EDGE,{"derivedFrom":subQ5}),1.0]])]});}
            var Q12;
            Q12=makeQuery(id+"F0.imprint","IMPRINT",FACE,{"disambiguationData":[TD([[makeQuery(id+"F0.imprint","IMPRINT",EDGE,{"derivedFrom":sQuery(id+"F0.wireOp",EDGE,"E21")}),1.0]])]});
            var Q13;
            Q13=makeQuery(id+"F0.imprint","IMPRINT",FACE,{"disambiguationData":[TD([[makeQuery(id+"F0.imprint","IMPRINT",EDGE,{"derivedFrom":sQuery(id+"F0.wireOp",EDGE,"E2.5")}),1.0]])]});
            var Q14;
            {var subQ0=sQuery(id+"F0.wireOp",EDGE,"E46");Q14=makeQuery(id+"F0.imprint","IMPRINT",FACE,{"disambiguationData":[TD([[makeQuery(id+"F0.imprint","IMPRINT",EDGE,{"derivedFrom":subQ0}),1.0]])]});}
            var Q15;
            {var subQ0=sQuery(id+"F0.wireOp",EDGE,"E14");var subQ1=sQuery(id+"F0.wireOp",EDGE,"E0.top");var subQ2=makeQuery(id+"F0.imprint","INTERSECT",VERTEX,{"derivedFrom":[subQ1,subQ0]});Q15=makeQuery(id+"F0.imprint","IMPRINT",FACE,{"disambiguationData":[TD([[makeQuery(id+"F0.imprint","IMPRINT",EDGE,{"disambiguationData":[TD([[subQ2,1.0]])],"derivedFrom":subQ1}),1.0]])]});}
            var Q16;
            {var subQ0=sQuery(id+"F0.wireOp",EDGE,"E103.1");Q16=makeQuery(id+"F0.imprint","IMPRINT",FACE,{"disambiguationData":[TD([[makeQuery(id+"F0.imprint","IMPRINT",EDGE,{"derivedFrom":subQ0}),-1.0]])]});}
            var Q17;
            Q17=makeQuery(id+"F0.imprint","IMPRINT",FACE,{"disambiguationData":[TD([[makeQuery(id+"F0.imprint","IMPRINT",EDGE,{"derivedFrom":sQuery(id+"F0.wireOp",EDGE,"E66.0")}),-1.0]])]});
            var Q18;
            Q18=makeQuery(id+"F0.imprint","IMPRINT",FACE,{"disambiguationData":[TD([[makeQuery(id+"F0.imprint","IMPRINT",EDGE,{"derivedFrom":sQuery(id+"F0.wireOp",EDGE,"E155")}),1.0]])]});
            var Q19;
            {var subQ3=sQuery(id+"F0.wireOp",EDGE,"d1deb05d-b4d8-4f16-9e59-166c224445ac.0");Q19=makeQuery(id+"F0.imprint","IMPRINT",FACE,{"disambiguationData":[TD([[makeQuery(id+"F0.imprint","IMPRINT",EDGE,{"derivedFrom":subQ3}),-1.0]])]});}
            var Q20;
            Q20=makeQuery(id+"F0.imprint","IMPRINT",FACE,{"disambiguationData":[TD([[makeQuery(id+"F0.imprint","IMPRINT",EDGE,{"derivedFrom":sQuery(id+"F0.wireOp",EDGE,"ZVYSHCS1-2Een-s850-w6lb-LcxjED9iCilX")}),-1.0]])]});
            var Q21;
            Q21=makeQuery(id+"F0.imprint","IMPRINT",FACE,{"disambiguationData":[TD([[makeQuery(id+"F0.imprint","IMPRINT",EDGE,{"derivedFrom":sQuery(id+"F0.wireOp",EDGE,"E157.trimOffspring")}),-1.0]])]});
            var Q22;
            {var subQ3=sQuery(id+"F0.wireOp",EDGE,"E193.0");Q22=makeQuery(id+"F0.imprint","IMPRINT",FACE,{"disambiguationData":[TD([[makeQuery(id+"F0.imprint","IMPRINT",EDGE,{"derivedFrom":subQ3}),-1.0]])]});}
            var Q23;
            {var subQ4=sQuery(id+"F0.wireOp",EDGE,"E178");Q23=makeQuery(id+"F0.imprint","IMPRINT",FACE,{"disambiguationData":[TD([[makeQuery(id+"F0.imprint","IMPRINT",EDGE,{"derivedFrom":subQ4}),-1.0]])]});}
            extrude(context, id + "F1", {"entities" : qUnion([Q0, Q1, Q2, Q3, Q4, Q5, Q6, Q7, Q8, Q9, Q10, Q11, Q12, Q13, Q14, Q15, Q16, Q17, Q18, Q19, Q20, Q21, Q22, Q23]), "depth" : 6 * mm, "offsetDistance" : 25 * mm});
        }
        {
            var Q0;
            Q0=makeQuery(id+"F1.opExtrude","CAP_FACE",FACE,{"disambiguationData":[OSD([sQuery(id+"F0.wireOp",EDGE,"E1"),sQuery(id+"F0.wireOp",EDGE,"E2.5"),sQuery(id+"F0.wireOp",EDGE,"E8"),sQuery(id+"F0.wireOp",EDGE,"E9.5"),sQuery(id+"F0.wireOp",EDGE,"E9.6"),sQuery(id+"F0.wireOp",EDGE,"E9.7"),sQuery(id+"F0.wireOp",EDGE,"E13"),sQuery(id+"F0.wireOp",EDGE,"E14"),sQuery(id+"F0.wireOp",EDGE,"E15"),sQuery(id+"F0.wireOp",EDGE,"E16"),sQuery(id+"F0.wireOp",EDGE,"E18"),sQuery(id+"F0.wireOp",EDGE,"E19"),sQuery(id+"F0.wireOp",EDGE,"E20"),sQuery(id+"F0.wireOp",EDGE,"E22"),sQuery(id+"F0.wireOp",EDGE,"E24"),sQuery(id+"F0.wireOp",EDGE,"E25"),sQuery(id+"F0.wireOp",EDGE,"E26"),sQuery(id+"F0.wireOp",EDGE,"E27"),sQuery(id+"F0.wireOp",EDGE,"E28"),sQuery(id+"F0.wireOp",EDGE,"E29"),sQuery(id+"F0.wireOp",EDGE,"E30.1"),sQuery(id+"F0.wireOp",EDGE,"E31.0"),sQuery(id+"F0.wireOp",EDGE,"E32"),sQuery(id+"F0.wireOp",EDGE,"E33"),sQuery(id+"F0.wireOp",EDGE,"E37"),sQuery(id+"F0.wireOp",EDGE,"E38"),sQuery(id+"F0.wireOp",EDGE,"E39"),sQuery(id+"F0.wireOp",EDGE,"E40"),sQuery(id+"F0.wireOp",EDGE,"E42"),sQuery(id+"F0.wireOp",EDGE,"E43"),sQuery(id+"F0.wireOp",EDGE,"E44"),sQuery(id+"F0.wireOp",EDGE,"E45"),sQuery(id+"F0.wireOp",EDGE,"E46"),sQuery(id+"F0.wireOp",EDGE,"E48.trimOffspring"),sQuery(id+"F0.wireOp",EDGE,"E49"),sQuery(id+"F0.wireOp",EDGE,"E50"),sQuery(id+"F0.wireOp",EDGE,"E53.trimOffspring"),sQuery(id+"F0.wireOp",EDGE,"E54"),sQuery(id+"F0.wireOp",EDGE,"E55"),sQuery(id+"F0.wireOp",EDGE,"E56"),sQuery(id+"F0.wireOp",EDGE,"E58"),sQuery(id+"F0.wireOp",EDGE,"E59"),sQuery(id+"F0.wireOp",EDGE,"E60.trimOffspring"),sQuery(id+"F0.wireOp",EDGE,"E62.0"),sQuery(id+"F0.wireOp",EDGE,"E64.trimOffspring"),sQuery(id+"F0.wireOp",EDGE,"E80.0"),sQuery(id+"F0.wireOp",EDGE,"E80.1"),sQuery(id+"F0.wireOp",EDGE,"E80.2"),sQuery(id+"F0.wireOp",EDGE,"E82"),sQuery(id+"F0.wireOp",EDGE,"E83.0"),sQuery(id+"F0.wireOp",EDGE,"E83.1"),sQuery(id+"F0.wireOp",EDGE,"E83.2"),sQuery(id+"F0.wireOp",EDGE,"E83.3"),sQuery(id+"F0.wireOp",EDGE,"E83.4"),sQuery(id+"F0.wireOp",EDGE,"E83.5"),sQuery(id+"F0.wireOp",EDGE,"E91.0"),sQuery(id+"F0.wireOp",EDGE,"E92.0"),sQuery(id+"F0.wireOp",EDGE,"E92.1"),sQuery(id+"F0.wireOp",EDGE,"E93"),sQuery(id+"F0.wireOp",EDGE,"E94.0"),sQuery(id+"F0.wireOp",EDGE,"E94.1"),sQuery(id+"F0.wireOp",EDGE,"E95.0"),sQuery(id+"F0.wireOp",EDGE,"E96"),sQuery(id+"F0.wireOp",EDGE,"E97"),sQuery(id+"F0.wireOp",EDGE,"E98.1"),sQuery(id+"F0.wireOp",EDGE,"E98.2"),sQuery(id+"F0.wireOp",EDGE,"E99"),sQuery(id+"F0.wireOp",EDGE,"E100"),sQuery(id+"F0.wireOp",EDGE,"E102"),sQuery(id+"F0.wireOp",EDGE,"E107.0"),sQuery(id+"F0.wireOp",EDGE,"E107.1"),sQuery(id+"F0.wireOp",EDGE,"E108.2"),sQuery(id+"F0.wireOp",EDGE,"E109.0"),sQuery(id+"F0.wireOp",EDGE,"E110"),sQuery(id+"F0.wireOp",EDGE,"E111"),sQuery(id+"F0.wireOp",EDGE,"E112"),sQuery(id+"F0.wireOp",EDGE,"E113.0"),sQuery(id+"F0.wireOp",EDGE,"E114"),sQuery(id+"F0.wireOp",EDGE,"E115"),sQuery(id+"F0.wireOp",EDGE,"E116"),sQuery(id+"F0.wireOp",EDGE,"E118"),sQuery(id+"F0.wireOp",EDGE,"E119"),sQuery(id+"F0.wireOp",EDGE,"E121"),sQuery(id+"F0.wireOp",EDGE,"E122.0"),sQuery(id+"F0.wireOp",EDGE,"E123"),sQuery(id+"F0.wireOp",EDGE,"E124"),sQuery(id+"F0.wireOp",EDGE,"E125"),sQuery(id+"F0.wireOp",EDGE,"E126"),sQuery(id+"F0.wireOp",EDGE,"E127"),sQuery(id+"F0.wireOp",EDGE,"E128.0"),sQuery(id+"F0.wireOp",EDGE,"E133.0"),sQuery(id+"F0.wireOp",EDGE,"E133.1"),sQuery(id+"F0.wireOp",EDGE,"E133.2"),sQuery(id+"F0.wireOp",EDGE,"E134.0"),sQuery(id+"F0.wireOp",EDGE,"E134.1"),sQuery(id+"F0.wireOp",EDGE,"E134.2"),sQuery(id+"F0.wireOp",EDGE,"E134.3"),sQuery(id+"F0.wireOp",EDGE,"E135.0"),sQuery(id+"F0.wireOp",EDGE,"E136"),sQuery(id+"F0.wireOp",EDGE,"E137.0"),sQuery(id+"F0.wireOp",EDGE,"E137.1"),sQuery(id+"F0.wireOp",EDGE,"E137.2"),sQuery(id+"F0.wireOp",EDGE,"E139.trimOffspring"),sQuery(id+"F0.wireOp",EDGE,"E141.0"),sQuery(id+"F0.wireOp",EDGE,"E141.1"),sQuery(id+"F0.wireOp",EDGE,"E142.0"),sQuery(id+"F0.wireOp",EDGE,"E142.1"),sQuery(id+"F0.wireOp",EDGE,"E143"),sQuery(id+"F0.wireOp",EDGE,"E144.0"),sQuery(id+"F0.wireOp",EDGE,"E145.0"),sQuery(id+"F0.wireOp",EDGE,"E146.0"),sQuery(id+"F0.wireOp",EDGE,"E147.0"),sQuery(id+"F0.wireOp",EDGE,"E148.0"),sQuery(id+"F0.wireOp",EDGE,"E148.1"),sQuery(id+"F0.wireOp",EDGE,"E151"),sQuery(id+"F0.wireOp",EDGE,"E152.trimOffspring"),sQuery(id+"F0.wireOp",EDGE,"E154.trimOffspring"),sQuery(id+"F0.wireOp",EDGE,"E156"),sQuery(id+"F0.wireOp",EDGE,"E158"),sQuery(id+"F0.wireOp",EDGE,"E159.0"),sQuery(id+"F0.wireOp",EDGE,"E160"),sQuery(id+"F0.wireOp",EDGE,"E161.0"),sQuery(id+"F0.wireOp",EDGE,"E162.0"),sQuery(id+"F0.wireOp",EDGE,"E163.0"),sQuery(id+"F0.wireOp",EDGE,"E173.0"),sQuery(id+"F0.wireOp",EDGE,"E174"),sQuery(id+"F0.wireOp",EDGE,"E175"),sQuery(id+"F0.wireOp",EDGE,"E176.0"),sQuery(id+"F0.wireOp",EDGE,"E177"),sQuery(id+"F0.wireOp",EDGE,"E179"),sQuery(id+"F0.wireOp",EDGE,"E183"),sQuery(id+"F0.wireOp",EDGE,"E184"),sQuery(id+"F0.wireOp",EDGE,"E186"),sQuery(id+"F0.wireOp",EDGE,"E189"),sQuery(id+"F0.wireOp",EDGE,"E190.0"),sQuery(id+"F0.wireOp",EDGE,"E191"),sQuery(id+"F0.wireOp",EDGE,"E193.0")])],"isStart":true});
            var sketch = newSketch(context, id + "F2", { "sketchPlane" : qUnion([Q0])});
            skLineSegment(sketch, "E198.0", {"start": v(-48, 48) * mm, "end": v(35.85, 48) * mm});
            skLineSegment(sketch, "E199.0", {"start": v(-48, -48) * mm, "end": v(-48, 48) * mm});
            skLineSegment(sketch, "E200.0", {"start": v(-26.62, -45.27) * mm, "end": v(37.1, -45.27) * mm});
            skLineSegment(sketch, "E201.0", {"start": v(-48, -48) * mm, "end": v(-26.62, -48) * mm});
            skLineSegment(sketch, "E202.0", {"start": v(-26.62, -45.27) * mm, "end": v(-26.62, -48) * mm});
            skLineSegment(sketch, "E203.0", {"start": v(37.1, -14.1) * mm, "end": v(37.1, -45.27) * mm});
            skLineSegment(sketch, "E204.0", {"start": v(37.1, -14.1) * mm, "end": v(40.44, -14.1) * mm});
            skLineSegment(sketch, "E205.0", {"start": v(40.44, -14.1) * mm, "end": v(40.44, 16.38) * mm});
            skLineSegment(sketch, "E206.0", {"start": v(38.44, 16.38) * mm, "end": v(17.19, 16.38) * mm});
            skLineSegment(sketch, "E207.0", {"start": v(17.19, 19.08) * mm, "end": v(35.9, 19.08) * mm});
            skLineSegment(sketch, "E208.0", {"start": v(17.19, 16.38) * mm, "end": v(17.19, 19.08) * mm});
            skLineSegment(sketch, "E209.0", {"start": v(36.05, 21.08) * mm, "end": v(36.05, 35.77) * mm});
            skLineSegment(sketch, "E210.0", {"start": v(36.05, 35.77) * mm, "end": v(35.85, 43.22) * mm});
            skLineSegment(sketch, "E211.0", {"start": v(35.85, 48) * mm, "end": v(35.85, 43.22) * mm});
            skLineSegment(sketch, "E212.0", {"start": v(35.9, 19.08) * mm, "end": v(36.05, 21.08) * mm});
            skLineSegment(sketch, "E213.0", {"start": v(40.44, 16.38) * mm, "end": v(38.44, 16.38) * mm});
            skSolve(sketch);
        }
        {
            var Q0;
            Q0 = qSketchRegion(id + "F2", true);
            extrude(context, id + "F3", {"entities" : qUnion([Q0]), "depth" : 2 * mm, "offsetDistance" : 25 * mm});
        }
    });
